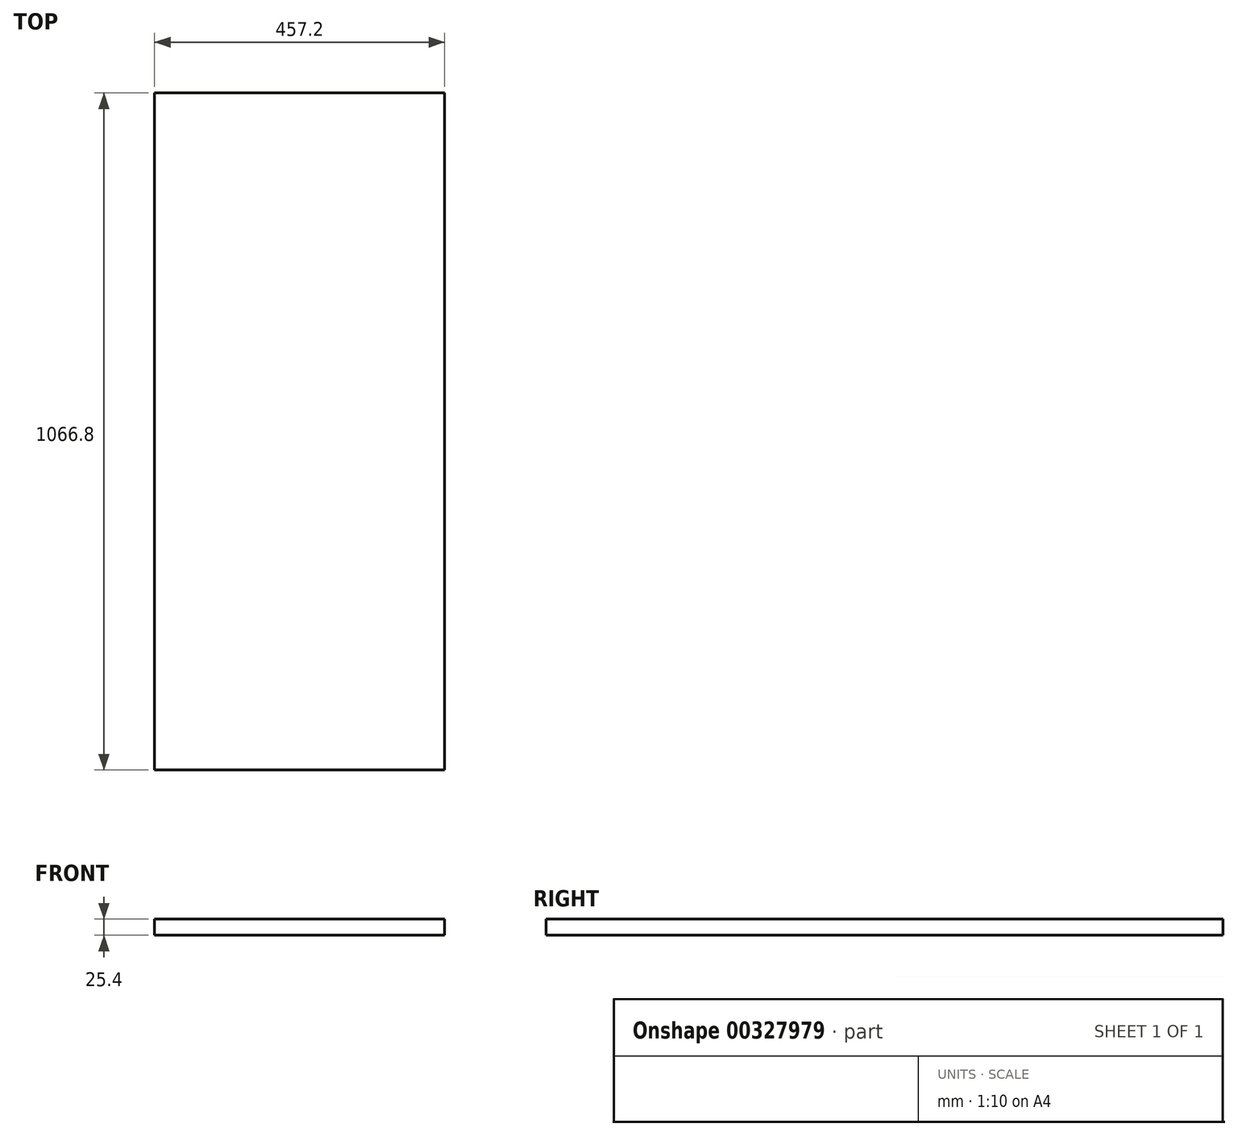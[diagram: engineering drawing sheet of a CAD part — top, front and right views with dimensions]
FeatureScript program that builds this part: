
annotation { "Feature Type Name" : "Feature", "Feature Type Description" : "" }
export const myFeature = defineFeature(function(context is Context, id is Id, definition is map)
    precondition{}
    {
        {
            var Q0;
            Q0=qCreatedBy(makeId("Top.planeOp"),FACE);
            var sketch = newSketch(context, id + "F0", { "sketchPlane" : qUnion([Q0])});
            skLineSegment(sketch, "E0", {"start": v(-381.54, -545.1) * mm, "end": v(-381.54, 521.7) * mm});
            skLineSegment(sketch, "E1", {"start": v(-381.54, 521.7) * mm, "end": v(75.66, 521.7) * mm});
            skLineSegment(sketch, "E2", {"start": v(75.66, 521.7) * mm, "end": v(75.66, -545.1) * mm});
            skLineSegment(sketch, "E3", {"start": v(75.66, -545.1) * mm, "end": v(-381.54, -545.1) * mm});
            skSolve(sketch);
        }
        {
            var Q0;
            Q0=makeQuery(id+"F0.imprint","IMPRINT",FACE,{"disambiguationData":[TD([[makeQuery(id+"F0.imprint","IMPRINT",EDGE,{"derivedFrom":sQuery(id+"F0.wireOp",EDGE,"E0")}),-1.0]])]});
            extrude(context, id + "F1", {"entities" : qUnion([Q0]), "depth" : 25.4 * mm});
        }
    });
